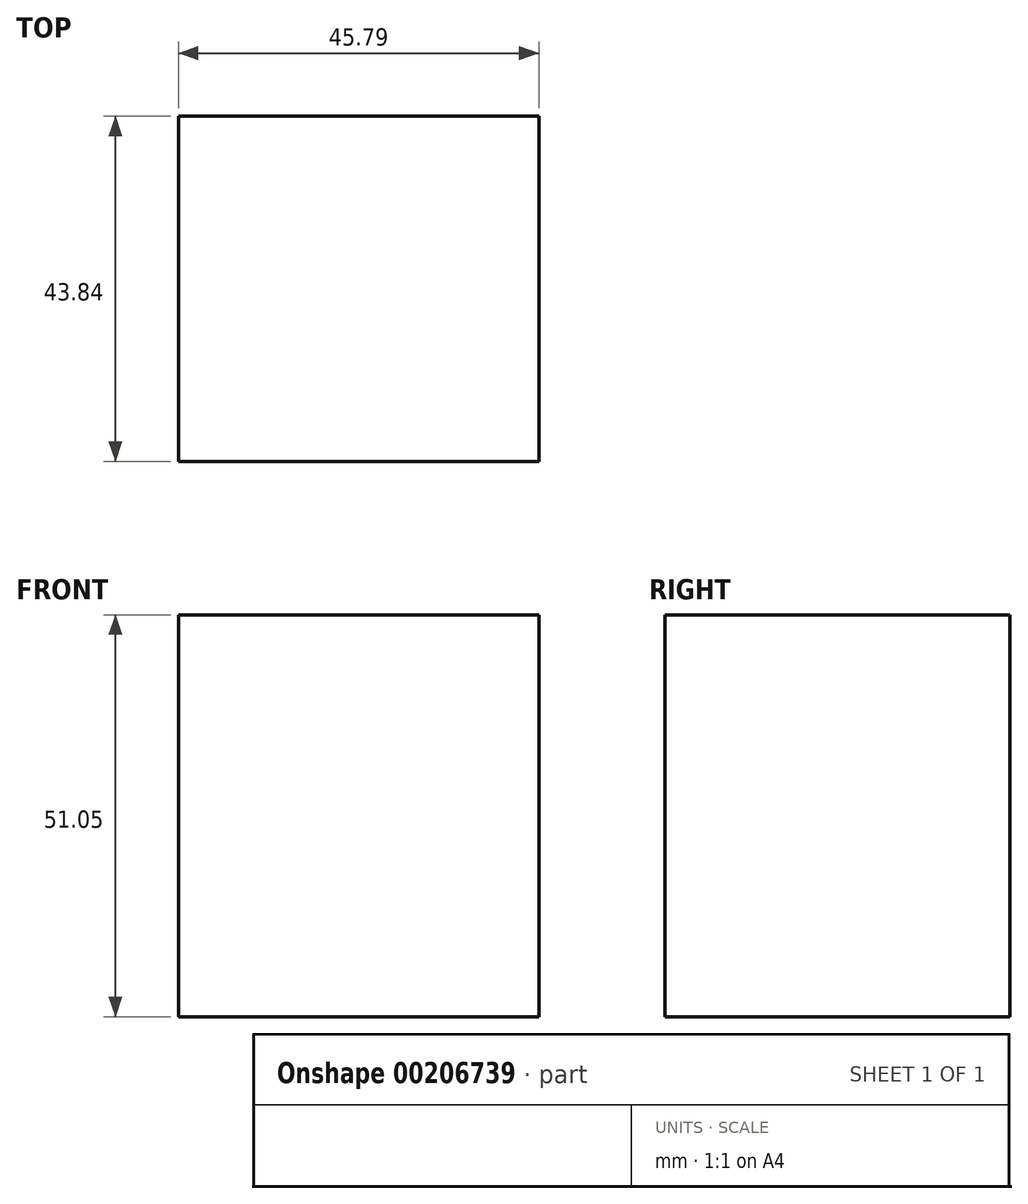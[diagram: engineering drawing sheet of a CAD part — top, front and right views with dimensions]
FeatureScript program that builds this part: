
annotation { "Feature Type Name" : "Feature", "Feature Type Description" : "" }
export const myFeature = defineFeature(function(context is Context, id is Id, definition is map)
    precondition{}
    {
        {
            var Q0;
            Q0=qCreatedBy(makeId("Top.planeOp"),FACE);
            var sketch = newSketch(context, id + "F0", { "sketchPlane" : qUnion([Q0])});
            skLineSegment(sketch, "E0.bottom", {"start": v(23.5, 23.02) * mm, "end": v(-22.29, 23.02) * mm});
            skLineSegment(sketch, "E0.top", {"start": v(23.5, -20.82) * mm, "end": v(-22.29, -20.82) * mm});
            skLineSegment(sketch, "E0.left", {"start": v(23.5, 23.02) * mm, "end": v(23.5, -20.82) * mm});
            skLineSegment(sketch, "E0.right", {"start": v(-22.29, 23.02) * mm, "end": v(-22.29, -20.82) * mm});
            skPoint(sketch, "E0.middle", {"position": v(0.6, 1.1) * mm});
            skSolve(sketch);
        }
        {
            var Q0;
            Q0 = qSketchRegion(id + "F0", true);
            extrude(context, id + "F1", {"entities" : qUnion([Q0]), "depth" : 51.05 * mm});
        }
    });
